# Revit family: Runoff-Teknion-CRHL_Runoff_Leg_Flush_to_Credenza-R2021
name_source: partatom
category: Furniture
units: mm (PartAtom-declared; Revit-internal decimal feet)

## family parameters
Always vertical = Yes
Cut with Voids When Loaded = No
OmniClass Number = 23.40.20.00
OmniClass Title = General Furniture and Specialties
Room Calculation Point = No
Shared = Yes
Work Plane-Based = No

## types (9) — shared parameters
Assembly Code = E2020200
Manufacturer = Teknion
Manufacturer Fax = 416.661.4586
Part Number = CRHL
Product Documentation Link = https://www.teknion.com
Product Line = Chronicle
Product Page URL = https://www.teknion.com
Series = Chronicle
Sustainability Data = https://www.teknion.com
URL = www.teknion.com
Unit Weight URL = http://www.teknion.com
Warranty = http://www.teknion.com
zero-valued in all types: Default Elevation

## per-type parameters (varying)
| type | Angled Leg | Description | Model | Modesty | Modesty Position | Post Leg | U-Leg |
| Partial Height Modesty, Inset Position, U-Leg Style | No | Chronicle Runoff, Leg, Flush to Credenza, Partial Height Modesty, Inset Position, U-Leg Style | CRHL__A_U | Yes | 4 " | No | Yes |
| Partial Height Modesty, Flush Position, U-Leg Style | No | Chronicle Runoff, Leg, Flush to Credenza, Partial Height Modesty, Flush Position, U-Leg Style | CRHL__B_U | Yes | 0 " | No | Yes |
| Partial Height Modesty, Inset Position, Post Leg Style | No | Chronicle Runoff, Leg, Flush to Credenza, Partial Height Modesty, Inset Position, Post Leg Style | CRHL__A_P | Yes | 4 " | Yes | No |
| Partial Height Modesty, Flush Position, Post Leg Style | No | Chronicle Runoff, Leg, Flush to Credenza, Partial Height Modesty, Flush Position, Post Leg Style | CRHL__B_P | Yes | 0 " | Yes | No |
| Partial Height Modesty, Inset Position, Angled Leg Style | Yes | Chronicle Runoff, Leg, Flush to Credenza, Partial Height Modesty, Inset Position, Angled Leg Style | CRHL__A_A | Yes | 4 " | No | No |
| Partial Height Modesty, Flush Position, Angled Leg Style | Yes | Chronicle Runoff, Leg, Flush to Credenza, Partial Height Modesty, Flush Position, Angled Leg Style | CRHL__B_A | Yes | 0 " | No | No |
| No Modesty, Angled Leg Style | Yes | Chronicle Runoff, Leg, Flush to Credenza, No Modesty, Angled Leg Style | CRHL__N_A | No | 0 " | No | No |
| No Modesty, U-Leg Style | No | Chronicle Runoff, Leg, Flush to Credenza, No Modesty, U-Leg Style | CRHL__N_U | No | 0 " | No | Yes |
| No Modesty, Post Leg Style | No | Chronicle Runoff, Leg, Flush to Credenza, No Modesty, Post Leg Style | CRHL__N_P | No | 0 " | Yes | No |

## geometry (parser evidence)
native form markers: Sweep x2
no freeform markers — native parametric forms only
